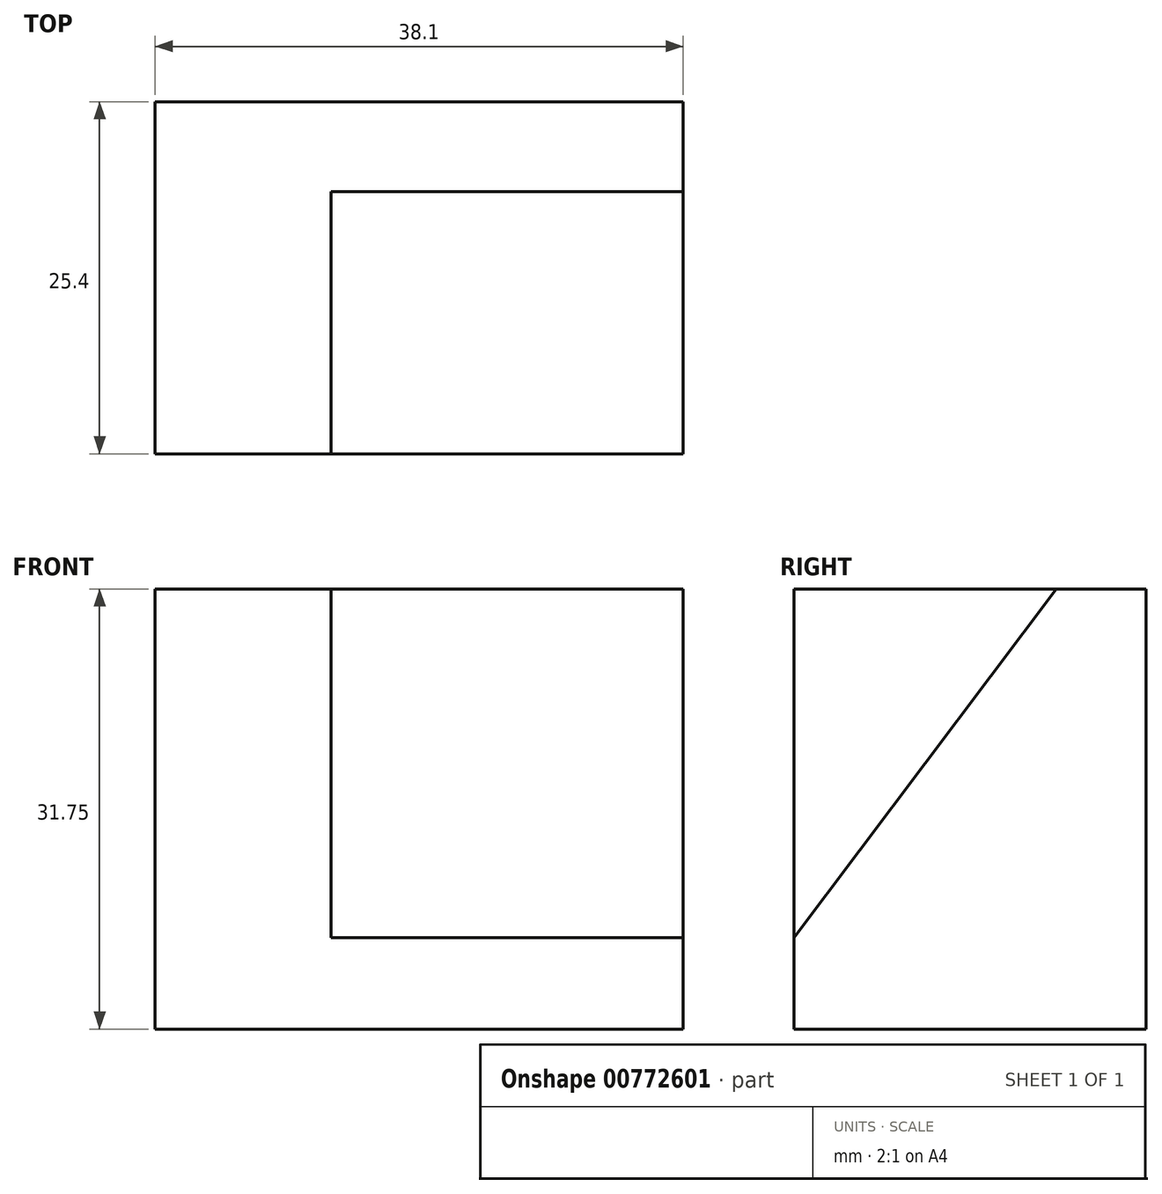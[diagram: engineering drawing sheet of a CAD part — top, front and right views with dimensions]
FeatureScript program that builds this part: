
annotation { "Feature Type Name" : "Feature", "Feature Type Description" : "" }
export const myFeature = defineFeature(function(context is Context, id is Id, definition is map)
    precondition{}
    {
        {
            var Q0;
            Q0=qCreatedBy(makeId("Front.planeOp"),FACE);
            var sketch = newSketch(context, id + "F0", { "sketchPlane" : qUnion([Q0])});
            skLineSegment(sketch, "E0", {"start": v(0, 0) * mm, "end": v(-38.1, 0) * mm});
            skLineSegment(sketch, "E1", {"start": v(-38.1, 0) * mm, "end": v(-38.1, 31.75) * mm});
            skLineSegment(sketch, "E2", {"start": v(-38.1, 31.75) * mm, "end": v(0, 31.75) * mm});
            skLineSegment(sketch, "E3", {"start": v(0, 31.75) * mm, "end": v(0, 0) * mm});
            skSolve(sketch);
        }
        {
            var Q0;
            Q0=makeQuery(id+"F0.imprint","IMPRINT",FACE,{"disambiguationData":[TD([[makeQuery(id+"F0.imprint","IMPRINT",EDGE,{"derivedFrom":sQuery(id+"F0.wireOp",EDGE,"E0")}),-1.0]])]});
            extrude(context, id + "F1", {"entities" : qUnion([Q0]), "depth" : 25.4 * mm, "offsetDistance" : 25.4 * mm});
        }
        {
            var Q0;
            Q0=makeQuery(id+"F1.opExtrude","SWEPT_FACE",FACE,{"disambiguationData":[OSD([sQuery(id+"F0.wireOp",EDGE,"E3")])]});
            var sketch = newSketch(context, id + "F2", { "sketchPlane" : qUnion([Q0])});
            skLineSegment(sketch, "E4", {"start": v(-25.4, 0) * mm, "end": v(-25.4, 6.35) * mm});
            skSolve(sketch);
        }
        {
            var Q0;
            {var subQ2=sQuery(id+"F2.wireOp",EDGE,"E4");Q0=makeQuery(id+"F2.imprint","IMPRINT",FACE,{"disambiguationData":[TD([[makeQuery(id+"F2.imprint","IMPRINT",EDGE,{"derivedFrom":subQ2}),1.0]])]});}
            var sketch = newSketch(context, id + "F3", { "sketchPlane" : qUnion([Q0])});
            skLineSegment(sketch, "E5", {"start": v(0, 31.95) * mm, "end": v(-6.35, 31.95) * mm});
            skLineSegment(sketch, "E6", {"start": v(-6.35, 31.95) * mm, "end": v(-25.5, 6.48) * mm});
            skSolve(sketch);
        }
        {
            var Q0;
            {var subQ0=sQuery(id+"F3.wireOp",EDGE,"E6");var subQ1=sQuery(id+"F0.wireOp",EDGE,"E3");var subQ2=makeQuery(id+"F1.opExtrude","SWEPT_EDGE",EDGE,{"disambiguationData":[OSD([sQuery(id+"F0.wireOp",EDGE,"E2"),subQ1])]});var subQ3=makeQuery(id+"F2.imprint","IMPRINT",EDGE,{"derivedFrom":subQ2});var subQ4=makeQuery(id+"F3.imprint","INTERSECT",VERTEX,{"derivedFrom":[subQ3,subQ0]});Q0=makeQuery(id+"F3.imprint","IMPRINT",FACE,{"disambiguationData":[TD([[makeQuery(id+"F3.imprint","IMPRINT",EDGE,{"disambiguationData":[TD([[subQ4,-1.0]])],"derivedFrom":subQ0}),-1.0]])]});}
            extrude(context, id + "F4", {"entities" : qUnion([Q0]), "operationType" : NewBodyOperationType.REMOVE, "oppositeDirection" : true, "depth" : 25.4 * mm, "offsetDistance" : 25.4 * mm});
        }
    });
